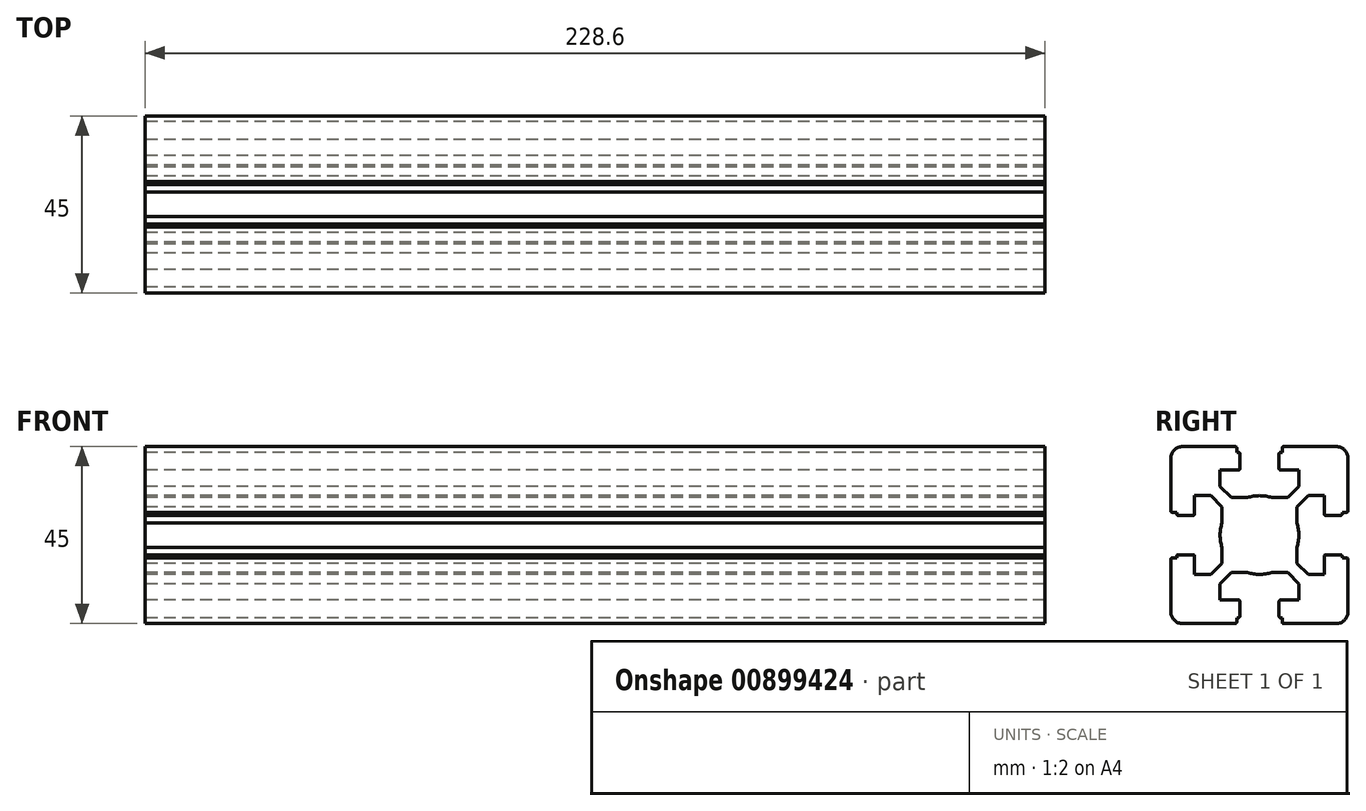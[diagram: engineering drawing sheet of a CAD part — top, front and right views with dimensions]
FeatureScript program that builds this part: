
annotation { "Feature Type Name" : "Feature", "Feature Type Description" : "" }
export const myFeature = defineFeature(function(context is Context, id is Id, definition is map)
    precondition{}
    {
        {
            var Q0;
            Q0=qCreatedBy(makeId("Right.planeOp"),FACE);
            var sketch = newSketch(context, id + "F0", { "sketchPlane" : qUnion([Q0])});
            skLineSegment(sketch, "E0", {"start": v(-20.09, -10.29) * mm, "end": v(-21.29, -10.29) * mm});
            skArc(sketch, "E1", {"start": v(-21.29, -10.29) * mm, "mid": v(-21.5, -10.38) * mm, "end": v(-21.59, -10.59) * mm});
            skLineSegment(sketch, "E2", {"start": v(-21.59, -10.59) * mm, "end": v(-21.59, -23.99) * mm});
            skArc(sketch, "E3", {"start": v(-21.59, -23.99) * mm, "mid": v(-20.7, -26.11) * mm, "end": v(-18.59, -26.99) * mm});
            skLineSegment(sketch, "E4", {"start": v(-18.59, -26.99) * mm, "end": v(-5.19, -26.99) * mm});
            skArc(sketch, "E5", {"start": v(-5.19, -26.99) * mm, "mid": v(-4.98, -26.9) * mm, "end": v(-4.89, -26.69) * mm});
            skLineSegment(sketch, "E6", {"start": v(-4.89, -26.69) * mm, "end": v(-4.89, -25.49) * mm});
            skLineSegment(sketch, "E7", {"start": v(-4.89, -25.49) * mm, "end": v(-4.39, -25.49) * mm});
            skArc(sketch, "E8", {"start": v(-4.39, -25.49) * mm, "mid": v(-4.18, -25.4) * mm, "end": v(-4.09, -25.19) * mm});
            skLineSegment(sketch, "E9", {"start": v(-4.09, -25.19) * mm, "end": v(-4.09, -21.29) * mm});
            skArc(sketch, "E10", {"start": v(-4.09, -21.29) * mm, "mid": v(-4.18, -21.08) * mm, "end": v(-4.39, -20.99) * mm});
            skLineSegment(sketch, "E11", {"start": v(-4.39, -20.99) * mm, "end": v(-9.14, -20.99) * mm});
            skLineSegment(sketch, "E12", {"start": v(-9.14, -20.99) * mm, "end": v(-9.14, -16.88) * mm});
            skLineSegment(sketch, "E13", {"start": v(-9.14, -16.88) * mm, "end": v(-6.25, -13.99) * mm});
            skLineSegment(sketch, "E14", {"start": v(-6.25, -13.99) * mm, "end": v(-2.21, -13.99) * mm});
            skArc(sketch, "E15", {"start": v(-2.21, -13.99) * mm, "mid": v(0.91, -14.49) * mm, "end": v(4.03, -13.99) * mm});
            skLineSegment(sketch, "E16", {"start": v(-20.09, -10.29) * mm, "end": v(-20.09, -9.79) * mm});
            skArc(sketch, "E17", {"start": v(-20.09, -9.79) * mm, "mid": v(-20, -9.58) * mm, "end": v(-19.79, -9.49) * mm});
            skLineSegment(sketch, "E18", {"start": v(-19.79, -9.49) * mm, "end": v(-15.89, -9.49) * mm});
            skArc(sketch, "E19", {"start": v(-15.89, -9.49) * mm, "mid": v(-15.68, -9.58) * mm, "end": v(-15.59, -9.79) * mm});
            skLineSegment(sketch, "E20", {"start": v(-15.59, -9.79) * mm, "end": v(-15.59, -14.54) * mm});
            skLineSegment(sketch, "E21", {"start": v(-15.59, -14.54) * mm, "end": v(-11.48, -14.54) * mm});
            skLineSegment(sketch, "E22", {"start": v(-11.48, -14.54) * mm, "end": v(-8.59, -11.65) * mm});
            skLineSegment(sketch, "E23", {"start": v(-8.59, -11.65) * mm, "end": v(-8.59, -7.61) * mm});
            skLineSegment(sketch, "E24", {"start": v(29.82, -4.49) * mm, "end": v(-31.05, -4.49) * mm});
            skLineSegment(sketch, "E25.MirrorCS", {"start": v(6.71, -25.49) * mm, "end": v(6.21, -25.49) * mm});
            skArc(sketch, "E26.MirrorCS", {"start": v(7.01, -26.99) * mm, "mid": v(6.8, -26.9) * mm, "end": v(6.71, -26.69) * mm});
            skLineSegment(sketch, "E27.MirrorCS", {"start": v(10.41, -11.65) * mm, "end": v(10.41, -7.61) * mm});
            skArc(sketch, "E28.MirrorCS", {"start": v(6.21, -25.49) * mm, "mid": v(6, -25.4) * mm, "end": v(5.91, -25.19) * mm});
            skLineSegment(sketch, "E29.MirrorCS", {"start": v(6.71, -26.69) * mm, "end": v(6.71, -25.49) * mm});
            skArc(sketch, "E30.MirrorCS", {"start": v(5.91, -21.29) * mm, "mid": v(6, -21.08) * mm, "end": v(6.21, -20.99) * mm});
            skLineSegment(sketch, "E31.MirrorCS", {"start": v(10.96, -16.88) * mm, "end": v(8.07, -13.99) * mm});
            skLineSegment(sketch, "E32.MirrorCS", {"start": v(13.3, -14.54) * mm, "end": v(10.41, -11.65) * mm});
            skLineSegment(sketch, "E33.MirrorCS", {"start": v(17.41, -14.54) * mm, "end": v(13.3, -14.54) * mm});
            skLineSegment(sketch, "E34.MirrorCS", {"start": v(17.41, -9.79) * mm, "end": v(17.41, -14.54) * mm});
            skLineSegment(sketch, "E35.MirrorCS", {"start": v(6.21, -20.99) * mm, "end": v(10.96, -20.99) * mm});
            skLineSegment(sketch, "E36.MirrorCS", {"start": v(8.07, -13.99) * mm, "end": v(4.03, -13.99) * mm});
            skArc(sketch, "E37.MirrorCS", {"start": v(4.03, -13.99) * mm, "mid": v(0.91, -14.49) * mm, "end": v(-2.21, -13.99) * mm});
            skLineSegment(sketch, "E38.MirrorCS", {"start": v(10.96, -20.99) * mm, "end": v(10.96, -16.88) * mm});
            skLineSegment(sketch, "E39.MirrorCS", {"start": v(5.91, -25.19) * mm, "end": v(5.91, -21.29) * mm});
            skArc(sketch, "E40.MirrorCS", {"start": v(23.41, -23.99) * mm, "mid": v(22.53, -26.11) * mm, "end": v(20.41, -26.99) * mm});
            skLineSegment(sketch, "E41.MirrorCS", {"start": v(20.41, -26.99) * mm, "end": v(7.01, -26.99) * mm});
            skLineSegment(sketch, "E42.MirrorCS", {"start": v(23.41, -10.59) * mm, "end": v(23.41, -23.99) * mm});
            skArc(sketch, "E43.MirrorCS", {"start": v(17.71, -9.49) * mm, "mid": v(17.5, -9.58) * mm, "end": v(17.41, -9.79) * mm});
            skArc(sketch, "E44.MirrorCS", {"start": v(23.11, -10.29) * mm, "mid": v(23.32, -10.38) * mm, "end": v(23.41, -10.59) * mm});
            skLineSegment(sketch, "E45.MirrorCS", {"start": v(21.91, -10.29) * mm, "end": v(21.91, -9.79) * mm});
            skLineSegment(sketch, "E46.MirrorCS", {"start": v(21.91, -10.29) * mm, "end": v(23.11, -10.29) * mm});
            skArc(sketch, "E47.MirrorCS", {"start": v(21.91, -9.79) * mm, "mid": v(21.82, -9.58) * mm, "end": v(21.61, -9.49) * mm});
            skLineSegment(sketch, "E48.MirrorCS", {"start": v(21.61, -9.49) * mm, "end": v(17.71, -9.49) * mm});
            skLineSegment(sketch, "E49.MirrorCS", {"start": v(6.71, 16.51) * mm, "end": v(6.21, 16.51) * mm});
            skArc(sketch, "E50.MirrorCS", {"start": v(-4.39, 16.51) * mm, "mid": v(-4.18, 16.42) * mm, "end": v(-4.09, 16.21) * mm});
            skLineSegment(sketch, "E51.MirrorCS", {"start": v(-4.89, 16.51) * mm, "end": v(-4.39, 16.51) * mm});
            skArc(sketch, "E52.MirrorCS", {"start": v(5.91, 12.31) * mm, "mid": v(6, 12.1) * mm, "end": v(6.21, 12.01) * mm});
            skLineSegment(sketch, "E53.MirrorCS", {"start": v(6.71, 17.71) * mm, "end": v(6.71, 16.51) * mm});
            skLineSegment(sketch, "E54.MirrorCS", {"start": v(-4.89, 17.71) * mm, "end": v(-4.89, 16.51) * mm});
            skArc(sketch, "E55.MirrorCS", {"start": v(-5.19, 18.01) * mm, "mid": v(-4.98, 17.92) * mm, "end": v(-4.89, 17.71) * mm});
            skArc(sketch, "E56.MirrorCS", {"start": v(-4.09, 12.31) * mm, "mid": v(-4.18, 12.1) * mm, "end": v(-4.39, 12.01) * mm});
            skArc(sketch, "E57.MirrorCS", {"start": v(7.01, 18.01) * mm, "mid": v(6.8, 17.92) * mm, "end": v(6.71, 17.71) * mm});
            skArc(sketch, "E58.MirrorCS", {"start": v(6.21, 16.51) * mm, "mid": v(6, 16.42) * mm, "end": v(5.91, 16.21) * mm});
            skArc(sketch, "E59.MirrorCS", {"start": v(23.11, 1.31) * mm, "mid": v(23.32, 1.4) * mm, "end": v(23.41, 1.61) * mm});
            skLineSegment(sketch, "E60.MirrorCS", {"start": v(21.91, 1.31) * mm, "end": v(21.91, 0.81) * mm});
            skArc(sketch, "E61.MirrorCS", {"start": v(-15.89, 0.51) * mm, "mid": v(-15.68, 0.6) * mm, "end": v(-15.59, 0.81) * mm});
            skArc(sketch, "E62.MirrorCS", {"start": v(-21.29, 1.31) * mm, "mid": v(-21.5, 1.4) * mm, "end": v(-21.59, 1.61) * mm});
            skArc(sketch, "E63.MirrorCS", {"start": v(17.71, 0.51) * mm, "mid": v(17.5, 0.6) * mm, "end": v(17.41, 0.81) * mm});
            skArc(sketch, "E64.MirrorCS", {"start": v(21.91, 0.81) * mm, "mid": v(21.82, 0.6) * mm, "end": v(21.61, 0.51) * mm});
            skLineSegment(sketch, "E65.MirrorCS", {"start": v(21.91, 1.31) * mm, "end": v(23.11, 1.31) * mm});
            skArc(sketch, "E66.MirrorCS", {"start": v(14.31, 5.31) * mm, "mid": v(14.1, 5.4) * mm, "end": v(14.01, 5.61) * mm});
            skArc(sketch, "E67.MirrorCS", {"start": v(-20.09, 0.81) * mm, "mid": v(-20, 0.6) * mm, "end": v(-19.79, 0.51) * mm});
            skLineSegment(sketch, "E68.MirrorCS", {"start": v(-20.09, 1.31) * mm, "end": v(-21.29, 1.31) * mm});
            skLineSegment(sketch, "E69.MirrorCS", {"start": v(-20.09, 1.31) * mm, "end": v(-20.09, 0.81) * mm});
            skLineSegment(sketch, "E70.MirrorCS", {"start": v(8.07, 5.01) * mm, "end": v(4.03, 5.01) * mm});
            skLineSegment(sketch, "E71.MirrorCS", {"start": v(-4.09, 16.21) * mm, "end": v(-4.09, 12.31) * mm});
            skLineSegment(sketch, "E72.MirrorCS", {"start": v(-9.14, 12.01) * mm, "end": v(-9.14, 7.9) * mm});
            skLineSegment(sketch, "E73.MirrorCS", {"start": v(-15.59, 5.56) * mm, "end": v(-11.48, 5.56) * mm});
            skLineSegment(sketch, "E74.MirrorCS", {"start": v(-4.39, 12.01) * mm, "end": v(-9.14, 12.01) * mm});
            skLineSegment(sketch, "E75.MirrorCS", {"start": v(-9.14, 7.9) * mm, "end": v(-6.25, 5.01) * mm});
            skLineSegment(sketch, "E76.MirrorCS", {"start": v(10.96, 12.01) * mm, "end": v(10.96, 7.9) * mm});
            skArc(sketch, "E77.MirrorCS", {"start": v(-21.59, 15.01) * mm, "mid": v(-20.7, 17.13) * mm, "end": v(-18.59, 18.01) * mm});
            skLineSegment(sketch, "E78.MirrorCS", {"start": v(23.41, 1.61) * mm, "end": v(23.41, 15.01) * mm});
            skLineSegment(sketch, "E79.MirrorCS", {"start": v(13.3, 5.56) * mm, "end": v(10.41, 2.67) * mm});
            skLineSegment(sketch, "E80.MirrorCS", {"start": v(-8.59, 2.67) * mm, "end": v(-8.59, -1.37) * mm});
            skLineSegment(sketch, "E81.MirrorCS", {"start": v(-15.59, 0.81) * mm, "end": v(-15.59, 5.56) * mm});
            skLineSegment(sketch, "E82.MirrorCS", {"start": v(10.41, 2.67) * mm, "end": v(10.41, -1.37) * mm});
            skLineSegment(sketch, "E83.MirrorCS", {"start": v(-18.59, 18.01) * mm, "end": v(-5.19, 18.01) * mm});
            skLineSegment(sketch, "E84.MirrorCS", {"start": v(10.96, 7.9) * mm, "end": v(8.07, 5.01) * mm});
            skLineSegment(sketch, "E85.MirrorCS", {"start": v(17.41, 5.56) * mm, "end": v(13.3, 5.56) * mm});
            skArc(sketch, "E86.MirrorCS", {"start": v(23.41, 15.01) * mm, "mid": v(22.53, 17.13) * mm, "end": v(20.41, 18.01) * mm});
            skLineSegment(sketch, "E87.MirrorCS", {"start": v(5.91, 16.21) * mm, "end": v(5.91, 12.31) * mm});
            skLineSegment(sketch, "E88.MirrorCS", {"start": v(17.41, 0.81) * mm, "end": v(17.41, 5.56) * mm});
            skLineSegment(sketch, "E89.MirrorCS", {"start": v(-11.48, 5.56) * mm, "end": v(-8.59, 2.67) * mm});
            skLineSegment(sketch, "E90.MirrorCS", {"start": v(-6.25, 5.01) * mm, "end": v(-2.21, 5.01) * mm});
            skLineSegment(sketch, "E91.MirrorCS", {"start": v(-21.59, 1.61) * mm, "end": v(-21.59, 15.01) * mm});
            skArc(sketch, "E92.MirrorCS", {"start": v(4.03, 5.01) * mm, "mid": v(0.91, 5.51) * mm, "end": v(-2.21, 5.01) * mm});
            skLineSegment(sketch, "E93.MirrorCS", {"start": v(6.21, 12.01) * mm, "end": v(10.96, 12.01) * mm});
            skArc(sketch, "E94.MirrorCS", {"start": v(-2.21, 5.01) * mm, "mid": v(0.91, 5.51) * mm, "end": v(4.03, 5.01) * mm});
            skLineSegment(sketch, "E95.MirrorCS", {"start": v(20.41, 18.01) * mm, "end": v(7.01, 18.01) * mm});
            skLineSegment(sketch, "E96.MirrorCS", {"start": v(-19.79, 0.51) * mm, "end": v(-15.89, 0.51) * mm});
            skLineSegment(sketch, "E97.MirrorCS", {"start": v(21.61, 0.51) * mm, "end": v(17.71, 0.51) * mm});
            skLineSegment(sketch, "E98.MirrorCS", {"start": v(0.91, -27.65) * mm, "end": v(0.91, 19.82) * mm});
            skArc(sketch, "E99", {"start": v(-8.59, -1.37) * mm, "mid": v(-9.09, -4.49) * mm, "end": v(-8.59, -7.61) * mm});
            skArc(sketch, "E100", {"start": v(10.41, -7.61) * mm, "mid": v(10.91, -4.49) * mm, "end": v(10.41, -1.37) * mm});
            skSolve(sketch);
        }
        {
            var Q0;
            Q0=qSketchRegion(id+"F0",true);
            extrude(context, id + "F1", {"entities" : qUnion([Q0]), "depth" : 228.6 * mm, "offsetDistance" : 25.4 * mm});
        }
    });
